# Revit family: 928-00-002-DN600-1200
name_source: partatom
category: Pipe Accessories
units: mm (PartAtom-declared; Revit-internal decimal feet)

## family parameters
Always vertical = Yes
Cut with Voids When Loaded = No
Part Type = Valve - Breaks Into
Round Connector Dimension = Use Diameter
Shared = No
Work Plane-Based = No

## types (7) — shared parameters
1 = 1 mm  [stored 0.00328084 ft]
5 = 5 mm  [stored 0.0164042 ft]
DN1000_PN25 = 928-A10-00-030020200
DN1200_PN25 = 928-A12-00-030020200
DN600_PN25 = 928-600-00-030010200
DN700_PN25 = 928-700-00-030010200
DN750_PN25 = 928-750-00-030010200
DN800_PN25 = 928-800-00-030010200
DN900_PN25 = 928-900-00-030020200
Description_ = AVK DISC CHECK VALVE, FLANGED, PN25
Raised_dis = 4 mm  [stored 0.0131234 ft]
Search_table = 928-00-002-DN600-1200
URL product pages = https://www.avkvalves.com
zero-valued in all types: Default Elevation

## per-type parameters (varying)
- DN600_PN25: A=460 mm; A-3=457 mm; B=218 mm; B-3=215 mm; Body_Arc=424 mm; Body_Rev1=54 mm  [stored 0.177165 ft]; Body_T=8 mm  [stored 0.0262467 ft]; Body_revolve=64 mm; Bore_R=300 mm; Bore_R_cut=302 mm; DN=600 mm; FL_R=420 mm; FL_T=36 mm  [stored 0.11811 ft]; FL_support1=70 mm; FL_support2=196 mm; FL_support3=87 mm; FL_support4=61 mm; Fillet=18 mm  [stored 0.0590551 ft]; Hole_R=29 mm; Inside_T=13 mm  [stored 0.0426509 ft]; Mid_FL=18 mm  [stored 0.0590551 ft]; Mid_FL+5=31 mm; PCD=385 mm; Raised_R=341 mm; Rib_L=54 mm  [stored 0.177165 ft]; Rib_T=70 mm; Slot_b=3 mm  [stored 0.00984252 ft]; Support_dim=44 mm; Support_dim1=220 mm; fillet_location=273 mm; logo=54 mm  [stored 0.177165 ft]; reference=304 mm; slot_L=7 mm  [stored 0.0229659 ft]
- DN700_PN25: A=560 mm; A-3=557 mm; B=250 mm; B-3=247 mm; Body_Arc=462 mm; Body_Rev1=60 mm  [stored 0.19685 ft]; Body_T=10 mm  [stored 0.0328084 ft]; Body_revolve=74 mm; Bore_R=350 mm; Bore_R_cut=352 mm; DN=700 mm; FL_R=455 mm; FL_T=40 mm  [stored 0.131234 ft]; FL_support1=81 mm; FL_support2=225 mm; FL_support3=100 mm; FL_support4=70 mm; Fillet=20 mm  [stored 0.0656168 ft]; Hole_R=29 mm; Inside_T=14 mm  [stored 0.0459318 ft]; Mid_FL=22 mm; Mid_FL+5=38 mm; PCD=420 mm; Raised_R=397 mm; Rib_L=60 mm  [stored 0.19685 ft]; Rib_T=80 mm; Slot_b=3 mm  [stored 0.00984252 ft]; Support_dim=54 mm  [stored 0.177165 ft]; Support_dim1=253 mm; fillet_location=318 mm; logo=63 mm  [stored 0.206693 ft]; reference=354 mm; slot_L=8 mm  [stored 0.0262467 ft]
- DN750_PN25: A=590 mm; A-3=587 mm; B=258 mm; B-3=255 mm; Body_Arc=495 mm; Body_Rev1=65 mm; Body_T=12 mm  [stored 0.0393701 ft]; Body_revolve=78 mm; Bore_R=375 mm; Bore_R_cut=377 mm; DN=750 mm; FL_R=480 mm; FL_T=43 mm  [stored 0.141076 ft]; FL_support1=86 mm; FL_support2=232 mm; FL_support3=103 mm; FL_support4=72 mm; Fillet=22 mm; Hole_R=32 mm; Inside_T=15 mm  [stored 0.0492126 ft]; Mid_FL=24 mm; Mid_FL+5=40 mm  [stored 0.131234 ft]; PCD=450 mm; Raised_R=420 mm; Rib_L=65 mm; Rib_T=82 mm; Slot_b=3 mm  [stored 0.00984252 ft]; Support_dim=57 mm  [stored 0.187008 ft]; Support_dim1=260 mm; fillet_location=336 mm; logo=64 mm; reference=379 mm; slot_L=9 mm  [stored 0.0295276 ft]
- DN800_PN25: A=590 mm; A-3=587 mm; B=258 mm; B-3=255 mm; Body_Arc=523 mm; Body_Rev1=65 mm; Body_T=14 mm  [stored 0.0459318 ft]; Body_revolve=78 mm; Bore_R=400 mm; Bore_R_cut=402 mm; DN=800 mm; FL_R=512 mm; FL_T=43 mm  [stored 0.141076 ft]; FL_support1=86 mm; FL_support2=232 mm; FL_support3=103 mm; FL_support4=72 mm; Fillet=22 mm; Hole_R=32 mm; Inside_T=15 mm  [stored 0.0492126 ft]; Mid_FL=24 mm; Mid_FL+5=40 mm  [stored 0.131234 ft]; PCD=475 mm; Raised_R=451 mm; Rib_L=65 mm; Rib_T=82 mm; Slot_b=3 mm  [stored 0.00984252 ft]; Support_dim=57 mm  [stored 0.187008 ft]; Support_dim1=260 mm; fillet_location=361 mm; logo=64 mm; reference=404 mm; slot_L=9 mm  [stored 0.0295276 ft]
- DN900_PN25: A=740 mm; A-3=737 mm; B=355 mm; B-3=352 mm; Body_Arc=578 mm; Body_Rev1=70 mm; Body_T=15 mm  [stored 0.0492126 ft]; Body_revolve=91 mm; Bore_R=450 mm; Bore_R_cut=452 mm; DN=900 mm; FL_R=562 mm; FL_T=47 mm; FL_support1=100 mm; FL_support2=320 mm; FL_support3=142 mm; FL_support4=99 mm; Fillet=23 mm; Hole_R=32 mm; Inside_T=16 mm  [stored 0.0524934 ft]; Mid_FL=30 mm  [stored 0.0984252 ft]; Mid_FL+5=50 mm  [stored 0.164042 ft]; PCD=525 mm; Raised_R=500 mm; Rib_L=70 mm; Rib_T=114 mm; Slot_b=4 mm  [stored 0.0131234 ft]; Support_dim=71 mm; Support_dim1=359 mm; fillet_location=400 mm; logo=89 mm; reference=454 mm; slot_L=9 mm  [stored 0.0295276 ft]
- DN1000_PN25: A=750 mm; A-3=747 mm; B=365 mm; B-3=362 mm; Body_Arc=644 mm; Body_Rev1=75 mm; Body_T=15 mm  [stored 0.0492126 ft]; Body_revolve=95 mm; Bore_R=500 mm; Bore_R_cut=502 mm; DN=1000 mm; FL_R=627 mm; FL_T=50 mm  [stored 0.164042 ft]; FL_support1=105 mm; FL_support2=329 mm; FL_support3=146 mm; FL_support4=102 mm; Fillet=25 mm  [stored 0.082021 ft]; Hole_R=36 mm  [stored 0.11811 ft]; Inside_T=18 mm  [stored 0.0590551 ft]; Mid_FL=30 mm  [stored 0.0984252 ft]; Mid_FL+5=51 mm; PCD=585 mm; Raised_R=556 mm; Rib_L=75 mm; Rib_T=117 mm; Slot_b=4 mm  [stored 0.0131234 ft]; Support_dim=72 mm; Support_dim1=369 mm; fillet_location=445 mm; logo=91 mm; reference=504 mm; slot_L=10 mm  [stored 0.0328084 ft]
- DN1200_PN25: A=945 mm; A-3=942 mm; B=450 mm; B-3=447 mm; Body_Arc=765 mm; Body_Rev1=86 mm; Body_T=18 mm  [stored 0.0590551 ft]; Body_revolve=114 mm; Bore_R=600 mm; Bore_R_cut=602 mm; DN=1200 mm; FL_R=743 mm; FL_T=57 mm  [stored 0.187008 ft]; FL_support1=125 mm; FL_support2=405 mm; FL_support3=180 mm; FL_support4=126 mm; Fillet=29 mm; Hole_R=36 mm  [stored 0.11811 ft]; Inside_T=20 mm  [stored 0.0656168 ft]; Mid_FL=38 mm; Mid_FL+5=64 mm; PCD=695 mm; Raised_R=664 mm; Rib_L=86 mm; Rib_T=144 mm; Slot_b=5 mm  [stored 0.0164042 ft]; Support_dim=91 mm; Support_dim1=455 mm; fillet_location=531 mm; logo=113 mm; reference=604 mm; slot_L=11 mm

note: [stored X ft] marks values corroborated as IEEE doubles in the binary element streams (Revit-internal decimal feet)

## geometry (parser evidence)
native form markers: Sweep x9
no freeform markers — native parametric forms only
